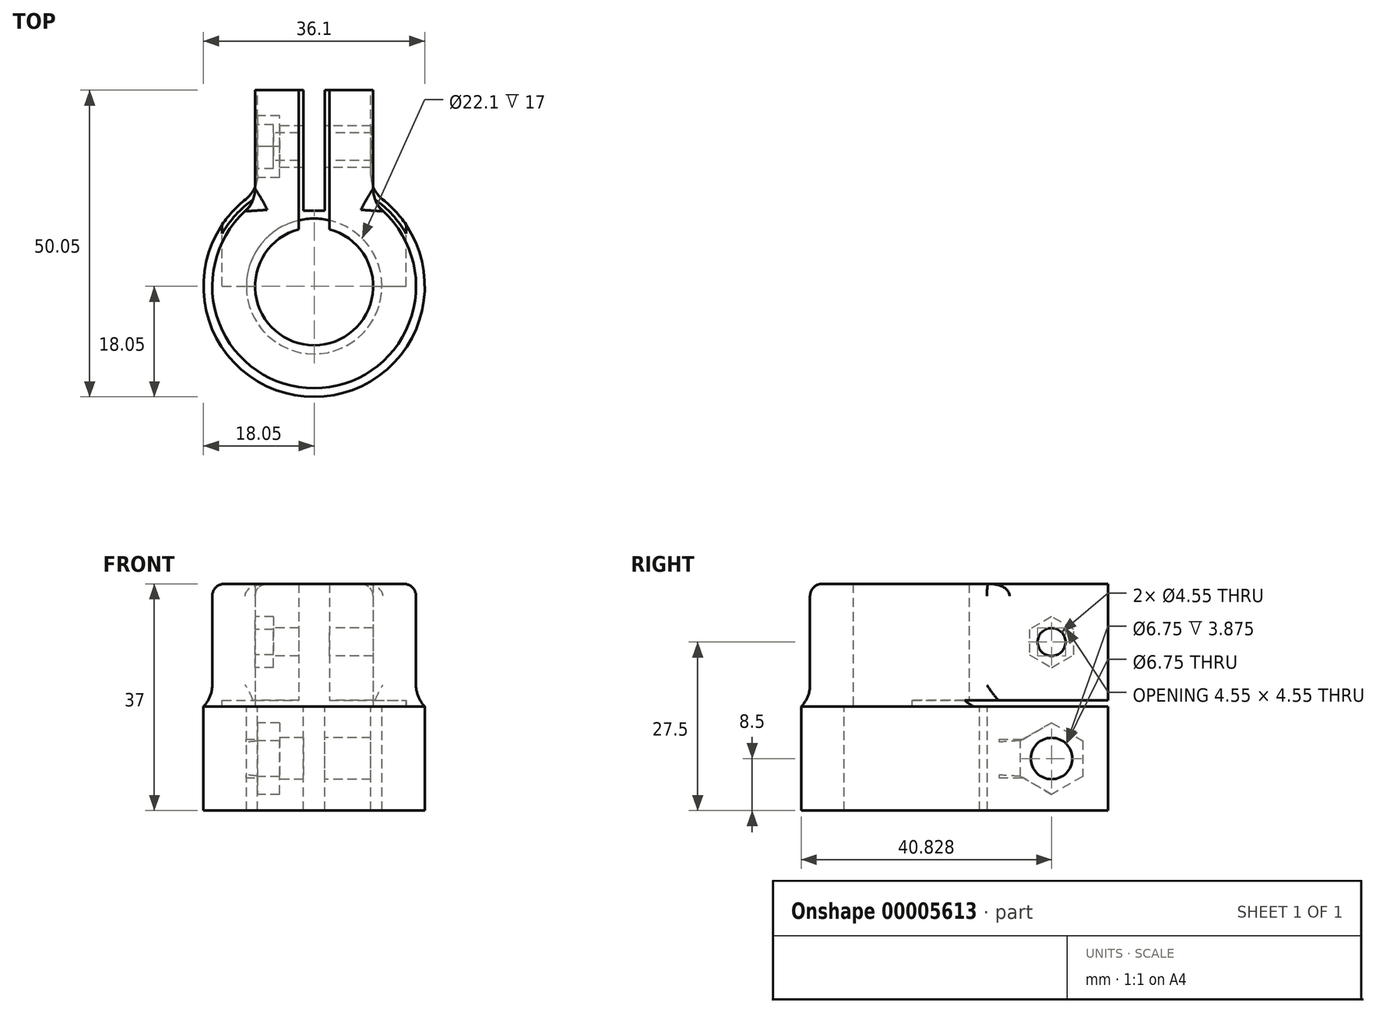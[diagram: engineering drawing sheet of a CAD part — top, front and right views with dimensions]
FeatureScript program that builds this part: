
annotation { "Feature Type Name" : "Feature", "Feature Type Description" : "" }
export const myFeature = defineFeature(function(context is Context, id is Id, definition is map)
    precondition{}
    {
        {
            var Q0;
            Q0=qCreatedBy(makeId("Top.planeOp"),FACE);
            var sketch = newSketch(context, id + "F0", { "sketchPlane" : qUnion([Q0])});
            skCircle(sketch, "E0", {"center": v(0, 0) * mm, "radius": 9.62 * mm});
            skLineSegment(sketch, "E1.bottom", {"start": v(-9.62, 0) * mm, "end": v(9.62, 0) * mm});
            skLineSegment(sketch, "E1.top", {"start": v(-9.63, 32) * mm, "end": v(9.63, 32) * mm});
            skLineSegment(sketch, "E1.left", {"start": v(-9.62, 0) * mm, "end": v(-9.63, 32) * mm});
            skLineSegment(sketch, "E1.right", {"start": v(9.63, 0) * mm, "end": v(9.62, 32) * mm});
            skLineSegment(sketch, "E2", {"start": v(0, -16.23) * mm, "end": v(0, 37.98) * mm, "construction": true});
            skLineSegment(sketch, "E3.rect.bottom", {"start": v(2.5, 32) * mm, "end": v(-2.5, 32) * mm});
            skLineSegment(sketch, "E3.rect.top", {"start": v(2.5, 0) * mm, "end": v(-2.5, 0) * mm});
            skLineSegment(sketch, "E3.rect.left", {"start": v(2.5, 32) * mm, "end": v(2.5, 0) * mm});
            skLineSegment(sketch, "E3.rect.right", {"start": v(-2.5, 32) * mm, "end": v(-2.5, 0) * mm});
            skPoint(sketch, "E3.rect.middle", {"position": v(0, 16) * mm});
            skCircle(sketch, "E4.0", {"center": v(0, 0) * mm, "radius": 16.62 * mm});
            skSolve(sketch);
        }
        {
            var Q0;
            {var subQ3=sQuery(id+"F0.wireOp",EDGE,"E1.right");var subQ5=sQuery(id+"F0.wireOp",EDGE,"E1.top");var subQ7=makeQuery(id+"F0.imprint","INTERSECT",VERTEX,{"derivedFrom":[subQ5,subQ3]});Q0=makeQuery(id+"F0.imprint","IMPRINT",FACE,{"disambiguationData":[TD([[makeQuery(id+"F0.imprint","IMPRINT",EDGE,{"disambiguationData":[TD([[subQ7,1.0]])],"derivedFrom":subQ3}),1.0]])]});}
            var Q1;
            {var subQ3=sQuery(id+"F0.wireOp",EDGE,"E1.left");var subQ5=sQuery(id+"F0.wireOp",EDGE,"E1.top");var subQ7=makeQuery(id+"F0.imprint","INTERSECT",VERTEX,{"derivedFrom":[subQ5,subQ3]});Q1=makeQuery(id+"F0.imprint","IMPRINT",FACE,{"disambiguationData":[TD([[makeQuery(id+"F0.imprint","IMPRINT",EDGE,{"disambiguationData":[TD([[subQ7,1.0]])],"derivedFrom":subQ3}),-1.0]])]});}
            var Q2;
            {var subQ0=sQuery(id+"F0.wireOp",EDGE,"E3.rect.right");var subQ3=sQuery(id+"F0.wireOp",EDGE,"E0");var subQ4=makeQuery(id+"F0.imprint","INTERSECT",VERTEX,{"derivedFrom":[subQ3,subQ0]});Q2=makeQuery(id+"F0.imprint","IMPRINT",FACE,{"disambiguationData":[TD([[makeQuery(id+"F0.imprint","IMPRINT",EDGE,{"disambiguationData":[TD([[subQ4,1.0]])],"derivedFrom":subQ0}),-1.0]])]});}
            var Q3;
            {var subQ1=sQuery(id+"F0.wireOp",EDGE,"E3.rect.left");var subQ5=sQuery(id+"F0.wireOp",EDGE,"E0");var subQ6=makeQuery(id+"F0.imprint","INTERSECT",VERTEX,{"derivedFrom":[subQ5,subQ1]});Q3=makeQuery(id+"F0.imprint","IMPRINT",FACE,{"disambiguationData":[TD([[makeQuery(id+"F0.imprint","IMPRINT",EDGE,{"disambiguationData":[TD([[subQ6,1.0]])],"derivedFrom":subQ1}),1.0]])]});}
            var Q4;
            {var subQ0=sQuery(id+"F0.wireOp",EDGE,"E4.0");var subQ3=sQuery(id+"F0.wireOp",EDGE,"E1.left");var subQ4=makeQuery(id+"F0.imprint","INTERSECT",VERTEX,{"derivedFrom":[subQ3,subQ0]});Q4=makeQuery(id+"F0.imprint","IMPRINT",FACE,{"disambiguationData":[TD([[makeQuery(id+"F0.imprint","IMPRINT",EDGE,{"disambiguationData":[TD([[subQ4,-1.0]])],"derivedFrom":subQ0}),1.0]])]});}
            extrude(context, id + "F1", {"entities" : qUnion([Q0, Q1, Q2, Q3, Q4]), "depth" : 20 * mm});
        }
        {
            var Q0;
            Q0=qCreatedBy(makeId("Top.planeOp"),FACE);
            var sketch = newSketch(context, id + "F2", { "sketchPlane" : qUnion([Q0])});
            skCircle(sketch, "E5", {"center": v(0, 0) * mm, "radius": 11.05 * mm});
            skLineSegment(sketch, "E6.rect.bottom", {"start": v(1.75, 12.32) * mm, "end": v(-1.75, 12.32) * mm});
            skLineSegment(sketch, "E6.rect.top", {"start": v(1.75, 32.8) * mm, "end": v(-1.75, 32.8) * mm});
            skLineSegment(sketch, "E6.rect.left", {"start": v(1.75, 12.32) * mm, "end": v(1.75, 32.8) * mm});
            skLineSegment(sketch, "E6.rect.right", {"start": v(-1.75, 12.32) * mm, "end": v(-1.75, 32.8) * mm});
            skPoint(sketch, "E6.rect.middle", {"position": v(0, 22.56) * mm});
            skLineSegment(sketch, "E7.rect.bottom", {"start": v(9.25, 12.32) * mm, "end": v(-9.25, 12.32) * mm});
            skLineSegment(sketch, "E7.rect.top", {"start": v(9.25, 32) * mm, "end": v(-9.25, 32) * mm});
            skLineSegment(sketch, "E7.rect.left", {"start": v(9.25, 12.32) * mm, "end": v(9.25, 32) * mm});
            skLineSegment(sketch, "E7.rect.right", {"start": v(-9.25, 12.32) * mm, "end": v(-9.25, 32) * mm});
            skPoint(sketch, "E7.rect.middle", {"position": v(0, 22.16) * mm});
            skCircle(sketch, "E8.0", {"center": v(0, 0) * mm, "radius": 18.05 * mm});
            skSolve(sketch);
        }
        {
            var Q0;
            {var subQ5=sQuery(id+"F2.wireOp",EDGE,"E5");var subQ7=sQuery(id+"F2.wireOp",EDGE,"E6.rect.right");var subQ9=makeQuery(id+"F2.imprint","INTERSECT",VERTEX,{"derivedFrom":[subQ5,subQ7]});Q0=makeQuery(id+"F2.imprint","IMPRINT",FACE,{"disambiguationData":[TD([[makeQuery(id+"F2.imprint","IMPRINT",EDGE,{"disambiguationData":[TD([[subQ9,-1.0]])],"derivedFrom":subQ5}),-1.0]])]});}
            var Q1;
            {var subQ0=sQuery(id+"F2.wireOp",EDGE,"E7.rect.left");var subQ1=sQuery(id+"F2.wireOp",EDGE,"f7832c3c-5660-40a9-af58-975c8304e058");var subQ2=makeQuery(id+"F2.imprint","INTERSECT",VERTEX,{"derivedFrom":[subQ1,subQ0]});Q1=makeQuery(id+"F2.imprint","IMPRINT",FACE,{"disambiguationData":[TD([[makeQuery(id+"F2.imprint","IMPRINT",EDGE,{"disambiguationData":[TD([[subQ2,-1.0]])],"derivedFrom":subQ1}),-1.0]])]});}
            var Q2;
            {var subQ3=sQuery(id+"F2.wireOp",EDGE,"E7.rect.bottom");var subQ8=sQuery(id+"F2.wireOp",EDGE,"E5");var subQ10=makeQuery(id+"F2.imprint","INTERSECT",VERTEX,{"disambiguationData":[OD(0.0)],"derivedFrom":[subQ8,subQ3]});Q2=makeQuery(id+"F2.imprint","IMPRINT",FACE,{"disambiguationData":[TD([[makeQuery(id+"F2.imprint","IMPRINT",EDGE,{"disambiguationData":[TD([[subQ10,1.0]])],"derivedFrom":subQ8}),-1.0]])]});}
            var Q3;
            {var subQ5=sQuery(id+"F2.wireOp",EDGE,"E5");var subQ7=sQuery(id+"F2.wireOp",EDGE,"E6.rect.left");var subQ9=makeQuery(id+"F2.imprint","INTERSECT",VERTEX,{"derivedFrom":[subQ5,subQ7]});Q3=makeQuery(id+"F2.imprint","IMPRINT",FACE,{"disambiguationData":[TD([[makeQuery(id+"F2.imprint","IMPRINT",EDGE,{"disambiguationData":[TD([[subQ9,1.0]])],"derivedFrom":subQ5}),-1.0]])]});}
            var Q4;
            {var subQ0=sQuery(id+"F2.wireOp",EDGE,"E7.rect.right");var subQ1=sQuery(id+"F2.wireOp",EDGE,"f7832c3c-5660-40a9-af58-975c8304e058");var subQ2=makeQuery(id+"F2.imprint","INTERSECT",VERTEX,{"derivedFrom":[subQ1,subQ0]});Q4=makeQuery(id+"F2.imprint","IMPRINT",FACE,{"disambiguationData":[TD([[makeQuery(id+"F2.imprint","IMPRINT",EDGE,{"disambiguationData":[TD([[subQ2,1.0]])],"derivedFrom":subQ1}),-1.0]])]});}
            var Q5;
            {var subQ1=sQuery(id+"F2.wireOp",EDGE,"E6.rect.left");var subQ5=sQuery(id+"F2.wireOp",EDGE,"E7.rect.top");var subQ7=makeQuery(id+"F2.imprint","INTERSECT",VERTEX,{"derivedFrom":[subQ1,subQ5]});Q5=makeQuery(id+"F2.imprint","IMPRINT",FACE,{"disambiguationData":[TD([[makeQuery(id+"F2.imprint","IMPRINT",EDGE,{"disambiguationData":[TD([[subQ7,1.0]])],"derivedFrom":subQ1}),-1.0]])]});}
            var Q6;
            {var subQ1=sQuery(id+"F2.wireOp",EDGE,"E6.rect.right");var subQ5=sQuery(id+"F2.wireOp",EDGE,"E7.rect.top");var subQ7=makeQuery(id+"F2.imprint","INTERSECT",VERTEX,{"derivedFrom":[subQ1,subQ5]});Q6=makeQuery(id+"F2.imprint","IMPRINT",FACE,{"disambiguationData":[TD([[makeQuery(id+"F2.imprint","IMPRINT",EDGE,{"disambiguationData":[TD([[subQ7,1.0]])],"derivedFrom":subQ1}),1.0]])]});}
            var Q7;
            {var subQ1=sQuery(id+"F2.wireOp",EDGE,"E6.rect.left");var subQ5=sQuery(id+"F2.wireOp",EDGE,"E7.rect.bottom");var subQ7=makeQuery(id+"F2.imprint","INTERSECT",VERTEX,{"derivedFrom":[subQ1,subQ5]});Q7=makeQuery(id+"F2.imprint","IMPRINT",FACE,{"disambiguationData":[TD([[makeQuery(id+"F2.imprint","IMPRINT",EDGE,{"disambiguationData":[TD([[subQ7,-1.0]])],"derivedFrom":subQ1}),-1.0]])]});}
            var Q8;
            {var subQ1=sQuery(id+"F2.wireOp",EDGE,"E6.rect.right");var subQ5=sQuery(id+"F2.wireOp",EDGE,"E7.rect.bottom");var subQ7=makeQuery(id+"F2.imprint","INTERSECT",VERTEX,{"derivedFrom":[subQ1,subQ5]});Q8=makeQuery(id+"F2.imprint","IMPRINT",FACE,{"disambiguationData":[TD([[makeQuery(id+"F2.imprint","IMPRINT",EDGE,{"disambiguationData":[TD([[subQ7,-1.0]])],"derivedFrom":subQ1}),1.0]])]});}
            extrude(context, id + "F3", {"entities" : qUnion([Q0, Q1, Q2, Q3, Q4, Q5, Q6, Q7, Q8]), "operationType" : NewBodyOperationType.ADD, "oppositeDirection" : true, "depth" : 17 * mm});
        }
        {
            var Q0;
            Q0=qCreatedBy(makeId("Right.planeOp"),FACE);
            var sketch = newSketch(context, id + "F4", { "sketchPlane" : qUnion([Q0])});
            skLineSegment(sketch, "E9.bottom", {"start": v(0, 0) * mm, "end": v(60, 0) * mm});
            skLineSegment(sketch, "E9.top", {"start": v(0, 1) * mm, "end": v(60, 1) * mm});
            skLineSegment(sketch, "E9.left", {"start": v(0, 0) * mm, "end": v(0, 1) * mm});
            skLineSegment(sketch, "E9.right", {"start": v(60, 0) * mm, "end": v(60, 1) * mm});
            skSolve(sketch);
        }
        {
            var Q0;
            Q0=makeQuery(id+"F4.imprint","IMPRINT",FACE,{"disambiguationData":[TD([[makeQuery(id+"F4.imprint","IMPRINT",EDGE,{"derivedFrom":sQuery(id+"F4.wireOp",EDGE,"E9.bottom")}),1.0]])]});
            extrude(context, id + "F5", {"entities" : qUnion([Q0]), "operationType" : NewBodyOperationType.REMOVE, "endBound" : BoundingType.SYMMETRIC, "oppositeDirection" : true, "depth" : 30 * mm});
        }
        {
            var Q0;
            Q0=makeQuery(id+"F1.opExtrude","SWEPT_FACE",FACE,{"disambiguationData":[OSD([sQuery(id+"F0.wireOp",EDGE,"E1.left")])]});
            var sketch = newSketch(context, id + "F6", { "sketchPlane" : qUnion([Q0])});
            skCircle(sketch, "E10", {"center": v(-22.78, 10.5) * mm, "radius": 2.27 * mm});
            skCircle(sketch, "E11", {"center": v(-22.78, -8.5) * mm, "radius": 3.38 * mm});
            skLineSegment(sketch, "E12.1", {"start": v(-32, 20) * mm, "end": v(-32, 1) * mm, "construction": true});
            skCircle(sketch, "E13.cCircle", {"center": v(-22.78, -8.5) * mm, "radius": 5.06 * mm, "construction": true});
            skLineSegment(sketch, "E13.0", {"start": v(-27.84, -11.42) * mm, "end": v(-27.84, -5.58) * mm});
            skLineSegment(sketch, "E13.1", {"start": v(-27.84, -5.58) * mm, "end": v(-22.78, -2.66) * mm});
            skLineSegment(sketch, "E13.2", {"start": v(-22.78, -2.66) * mm, "end": v(-17.72, -5.58) * mm});
            skLineSegment(sketch, "E13.3", {"start": v(-17.72, -5.58) * mm, "end": v(-17.72, -11.42) * mm});
            skLineSegment(sketch, "E13.4", {"start": v(-17.72, -11.42) * mm, "end": v(-22.78, -14.34) * mm});
            skLineSegment(sketch, "E13.5", {"start": v(-22.78, -14.34) * mm, "end": v(-27.84, -11.42) * mm});
            skPoint(sketch, "E13.0.midPoint", {"position": v(-27.84, -8.5) * mm});
            skCircle(sketch, "E14.cCircle", {"center": v(-22.78, 10.5) * mm, "radius": 3.6 * mm, "construction": true});
            skLineSegment(sketch, "E14.0", {"start": v(-26.38, 8.42) * mm, "end": v(-26.38, 12.58) * mm});
            skLineSegment(sketch, "E14.1", {"start": v(-26.38, 12.58) * mm, "end": v(-22.78, 14.66) * mm});
            skLineSegment(sketch, "E14.2", {"start": v(-22.78, 14.66) * mm, "end": v(-19.18, 12.58) * mm});
            skLineSegment(sketch, "E14.3", {"start": v(-19.18, 12.58) * mm, "end": v(-19.18, 8.42) * mm});
            skLineSegment(sketch, "E14.4", {"start": v(-19.18, 8.42) * mm, "end": v(-22.78, 6.34) * mm});
            skLineSegment(sketch, "E14.5", {"start": v(-22.78, 6.34) * mm, "end": v(-26.38, 8.42) * mm});
            skPoint(sketch, "E14.0.midPoint", {"position": v(-26.38, 10.5) * mm});
            skLineSegment(sketch, "E15", {"start": v(-13.56, 1) * mm, "end": v(-32, 20) * mm, "construction": true});
            skSolve(sketch);
        }
        {
            var Q0;
            Q0=makeQuery(id+"F6.imprint","IMPRINT",FACE,{"disambiguationData":[TD([[makeQuery(id+"F6.imprint","IMPRINT",EDGE,{"derivedFrom":sQuery(id+"F6.wireOp",EDGE,"E10")}),1.0]])]});
            var Q1;
            Q1=makeQuery(id+"F6.imprint","IMPRINT",FACE,{"disambiguationData":[TD([[makeQuery(id+"F6.imprint","IMPRINT",EDGE,{"derivedFrom":sQuery(id+"F6.wireOp",EDGE,"E11")}),1.0]])]});
            extrude(context, id + "F7", {"entities" : qUnion([Q0, Q1]), "operationType" : NewBodyOperationType.REMOVE, "oppositeDirection" : true, "depth" : 25.5 * mm});
        }
        {
            var Q0;
            Q0=makeQuery(id+"F6.imprint","IMPRINT",FACE,{"disambiguationData":[TD([[makeQuery(id+"F6.imprint","IMPRINT",EDGE,{"derivedFrom":sQuery(id+"F6.wireOp",EDGE,"E11")}),-1.0]])]});
            extrude(context, id + "F8", {"entities" : qUnion([Q0]), "operationType" : NewBodyOperationType.REMOVE, "oppositeDirection" : true, "depth" : 4 * mm});
        }
        {
            var Q0;
            Q0=makeQuery(id+"F6.imprint","IMPRINT",FACE,{"disambiguationData":[TD([[makeQuery(id+"F6.imprint","IMPRINT",EDGE,{"derivedFrom":sQuery(id+"F6.wireOp",EDGE,"E10")}),-1.0]])]});
            extrude(context, id + "F9", {"entities" : qUnion([Q0]), "operationType" : NewBodyOperationType.REMOVE, "oppositeDirection" : true, "depth" : 3 * mm});
        }
        {
            var Q0;
            Q0=makeQuery(id+"F1.opExtrude","CAP_EDGE",EDGE,{"disambiguationData":[OSD([sQuery(id+"F0.wireOp",EDGE,"E4.0")])],"isStart":true});
            fillet(context, id + "F10", {"entities" : qUnion([Q0]), "radius" : 5 * mm, "tangentPropagation" : true, "allowEdgeOverflow" : false});
        }
        {
            var Q0;
            Q0=makeQuery(id+"F1.opExtrude","CAP_EDGE",EDGE,{"disambiguationData":[OSD([sQuery(id+"F0.wireOp",EDGE,"E4.0")])],"isStart":false});
            var Q1;
            Q1=makeQuery(id+"F1.opExtrude","CAP_EDGE",EDGE,{"disambiguationData":[OSD([sQuery(id+"F0.wireOp",EDGE,"E1.right")])],"isStart":false});
            var Q2;
            Q2=makeQuery(id+"F1.opExtrude","CAP_EDGE",EDGE,{"disambiguationData":[OSD([sQuery(id+"F0.wireOp",EDGE,"E1.left")])],"isStart":false});
            fillet(context, id + "F11", {"entities" : qUnion([Q0, Q1, Q2]), "radius" : 2 * mm, "tangentPropagation" : true, "allowEdgeOverflow" : false});
        }
        {
            var Q0;
            Q0=makeQuery(id+"F1.opExtrude","SWEPT_EDGE",EDGE,{"disambiguationData":[OSD([sQuery(id+"F0.wireOp",EDGE,"E1.right"),sQuery(id+"F0.wireOp",EDGE,"E4.0")])]});
            var Q1;
            Q1=makeQuery(id+"F3.opExtrude","SWEPT_EDGE",EDGE,{"disambiguationData":[OSD([sQuery(id+"F2.wireOp",EDGE,"E7.rect.left"),sQuery(id+"F2.wireOp",EDGE,"E8.0")])]});
            var Q2;
            Q2=makeQuery(id+"F1.opExtrude","SWEPT_EDGE",EDGE,{"disambiguationData":[OSD([sQuery(id+"F0.wireOp",EDGE,"E1.left"),sQuery(id+"F0.wireOp",EDGE,"E4.0")])]});
            var Q3;
            Q3=makeQuery(id+"F3.opExtrude","SWEPT_EDGE",EDGE,{"disambiguationData":[OSD([sQuery(id+"F2.wireOp",EDGE,"E7.rect.right"),sQuery(id+"F2.wireOp",EDGE,"E8.0")])]});
            fillet(context, id + "F12", {"entities" : qUnion([Q0, Q1, Q2, Q3]), "radius" : 5 * mm, "tangentPropagation" : true, "allowEdgeOverflow" : false});
        }
    });
